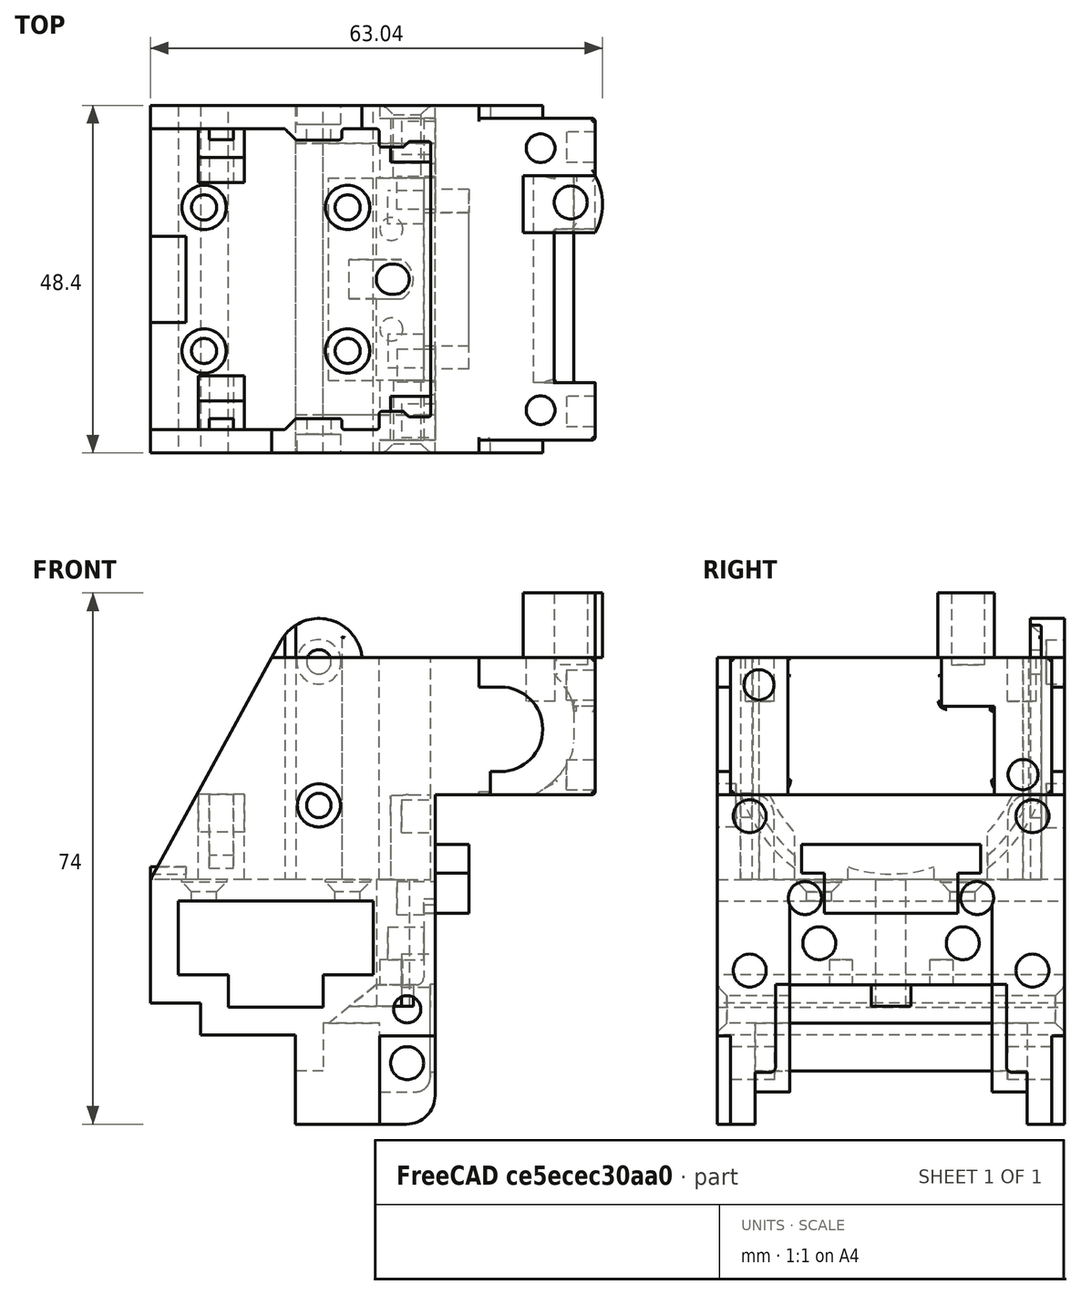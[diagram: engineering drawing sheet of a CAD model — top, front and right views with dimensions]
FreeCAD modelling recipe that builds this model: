
FCSTD DOCUMENT  (FreeCAD 1.0R38641 +468 (Git))
Label: k1_toolhead
License: All rights reserved
LicenseURL: https://en.wikipedia.org/wiki/All_rights_reserved
objects: App::Link×3, Part::Feature×1, PartDesign::FeatureBase×1, PartDesign::Body×1, App::Part×1
note: 4 computed .brp shape members not serialized (recipe doc carries the construction recipe); baked Part::Feature solids carry a one-line shape summary decoded from their .brp
EXTERNAL_REF file=cad_mgn12h_block.FCStd obj=Body
EXTERNAL_REF file=cad_extruder.FCStd obj=K1_Extruder_Assembly_v25
EXTERNAL_REF file=cad_hotend.FCStd obj=K1_Hotend

FEATURE [Part::Feature] Part__Feature  label="step"
  shape: bbox 63.04 x 48.4 x 74 mm, 296 faces (baked)
FEATURE [PartDesign::FeatureBase] BaseFeature
  BaseFeature = -> Part__Feature
  Suppressed = false
FEATURE [PartDesign::Body] Body  label="k1_toolhead"
  AllowCompound = false
  BaseFeature = -> Part__Feature
  Group = -> [BaseFeature]
  Origin = -> Origin001
  Tip = -> BaseFeature
FEATURE [App::Link] Link  label="cad_mgn12_link"
  LinkPlacement = pos=(-0.489994,-22.7,31.1) rot=(0.707107,0.707107,0;3.14159rad)
  LinkedObject = -> <external cad_mgn12h_block.FCStd>#Body
  Placement = pos=(-0.489994,-22.7,31.1) rot=(0.707107,0.707107,0;3.14159rad)
FEATURE [App::Link] Link001  label="cad_extruder_link"
  LinkPlacement = pos=(2.3,-0.3,53.5) rot=(0,0,1;1.5708rad)
  LinkedObject = -> <external cad_extruder.FCStd>#K1_Extruder_Assembly_v25
  Placement = pos=(2.3,-0.3,53.5) rot=(0,0,1;1.5708rad)
FEATURE [App::Link] Link002  label="cad_hotend_link"
  LinkedObject = -> <external cad_hotend.FCStd>#K1_Hotend
FEATURE [App::Part] Part  label="k1_toolhead_part"
  Group = -> [Body,Link,Link001,Link002]
  Origin = -> Origin

RESOLVED EXTERNAL PARTS (link-assembly join: the EXTERNAL_REF files above that resolve inside this repo's crawl, each included once):
---- part cad_mgn12h_block.FCStd = doc fcstd_671538b6926e ----
FCSTD DOCUMENT  (FreeCAD 1.0R38641 +468 (Git))
Label: cad_mgn12h_block
License: All rights reserved
LicenseURL: https://en.wikipedia.org/wiki/All_rights_reserved
objects: Sketcher::SketchObject×3, PartDesign::Pocket×2, PartDesign::Pad×1, PartDesign::Body×1
note: 16 computed .brp shape members not serialized (recipe doc carries the construction recipe); baked Part::Feature solids carry a one-line shape summary decoded from their .brp

FEATURE [Sketcher::SketchObject] Sketch
  ArcFitTolerance = 0
  AttachmentSupport = -> [YZ_Plane]
  FullyConstrained = true
  MakeInternals = false
  MapMode = 5
  Placement = pos=(0,0,0) rot=(0.57735,0.57735,0.57735;2.0944rad)
  sketch-geometry (4):
    g0: LineSegment StartX=13.5 StartY=0 StartZ=0 EndX=-13.5 EndY=-1e-16 EndZ=0
    g1: LineSegment StartX=-13.5 StartY=-1e-16 StartZ=0 EndX=-13.5 EndY=10 EndZ=0
    g2: LineSegment StartX=-13.5 StartY=10 StartZ=0 EndX=13.5 EndY=10 EndZ=0
    g3: LineSegment StartX=13.5 StartY=10 StartZ=0 EndX=13.5 EndY=0 EndZ=0
  constraints (11):
    c: Coincident(g0,g1)
    c: Coincident(g1,g2)
    c: Coincident(g2,g3)
    c: Coincident(g3,g0)
    c: Horizontal(g2)
    c: Vertical(g1)
    c: Vertical(g3)
    c: PointOnObject(g0,g-1)
    c: Symmetric(g0,g0,g-2)
    c: Distance(g2) = 27
    c: Distance(g1) = 10
FEATURE [PartDesign::Pad] Pad
  Direction = (1,0,0)
  Length = 45.4
  Length2 = 10
  Placement = pos=(0,0,0) rot=(1,1,1;2.0944rad)
  Profile = -> Sketch
  ReferenceAxis = -> Sketch [N_Axis]
  Suppressed = false
  Type = 0
FEATURE [Sketcher::SketchObject] Sketch001
  ArcFitTolerance = 0
  AttachmentSupport = -> [Pad]
  FullyConstrained = true
  MakeInternals = false
  MapMode = 5
  Placement = pos=(0,0,0) rot=(0.707107,0.707107,0;3.14159rad)
  sketch-geometry (8):
    g0: LineSegment [constr] StartX=-10 StartY=32.7 StartZ=0 EndX=10 EndY=32.7 EndZ=0
    g1: LineSegment [constr] StartX=10 StartY=32.7 StartZ=0 EndX=10 EndY=12.7 EndZ=0
    g2: LineSegment [constr] StartX=10 StartY=12.7 StartZ=0 EndX=-10 EndY=12.7 EndZ=0
    g3: LineSegment [constr] StartX=-10 StartY=12.7 StartZ=0 EndX=-10 EndY=32.7 EndZ=0
    g4: Circle CenterX=-10 CenterY=32.7 CenterZ=0 NormalX=0 NormalY=0 NormalZ=1 AngleXU=0 Radius=1.5
    g5: Circle CenterX=10 CenterY=32.7 CenterZ=0 NormalX=0 NormalY=0 NormalZ=1 AngleXU=0 Radius=1.5
    g6: Circle CenterX=10 CenterY=12.7 CenterZ=0 NormalX=0 NormalY=0 NormalZ=1 AngleXU=0 Radius=1.5
    g7: Circle CenterX=-10 CenterY=12.7 CenterZ=0 NormalX=0 NormalY=0 NormalZ=1 AngleXU=0 Radius=1.5
  constraints (19):
    c: Coincident(g0,g1)
    c: Coincident(g1,g2)
    c: Coincident(g2,g3)
    c: Coincident(g3,g0)
    c: Horizontal(g2)
    c: Vertical(g1)
    c: Vertical(g3)
    c: Symmetric(g0,g0,g-2)
    c: Distance(g0) = 20
    c: Distance(g1) = 20
    c: DistanceY(g-1,g2) = 12.7
    c: Coincident(g4,g0)
    c: Coincident(g5,g0)
    c: Coincident(g6,g1)
    c: Coincident(g7,g2)
    c: Equal(g7,g6)
    c: Equal(g6,g5)
    c: Equal(g5,g4)
    c: Radius(g4) = 1.5
FEATURE [PartDesign::Pocket] Pocket
  BaseFeature = -> Pad
  Direction = (0,0,1)
  Length = 5
  Length2 = 5
  Placement = pos=(0,0,0) rot=(1,1,1;2.0944rad)
  Profile = -> Sketch001
  ReferenceAxis = -> Sketch001 [N_Axis]
  Suppressed = false
  Type = 0
FEATURE [Sketcher::SketchObject] Sketch002
  ArcFitTolerance = 0
  AttachmentSupport = -> [Pocket]
  ExternalGeometry = -> [Pocket]
  FullyConstrained = true
  MakeInternals = false
  MapMode = 5
  Placement = pos=(0,0,0) rot=(0.57735,0.57735,-0.57735;4.18879rad)
  sketch-geometry (4):
    g0: LineSegment StartX=-6 StartY=-10 StartZ=0 EndX=6 EndY=-10 EndZ=0
    g1: LineSegment StartX=6 StartY=-10 StartZ=0 EndX=6 EndY=-5 EndZ=0
    g2: LineSegment StartX=6 StartY=-5 StartZ=0 EndX=-6 EndY=-5 EndZ=0
    g3: LineSegment StartX=-6 StartY=-5 StartZ=0 EndX=-6 EndY=-10 EndZ=0
  constraints (11):
    c: Coincident(g0,g1)
    c: Coincident(g1,g2)
    c: Coincident(g2,g3)
    c: Coincident(g3,g0)
    c: Horizontal(g0)
    c: Vertical(g1)
    c: Vertical(g3)
    c: PointOnObject(g0,g-3)
    c: Symmetric(g2,g1,g-2)
    c: Distance(g1) = 5
    c: Distance(g2) = 12
FEATURE [PartDesign::Pocket] Pocket001
  BaseFeature = -> Pocket
  Direction = (1,0,0)
  Length = 5
  Length2 = 5
  Placement = pos=(0,0,0) rot=(1,1,1;2.0944rad)
  Profile = -> Sketch002
  ReferenceAxis = -> Sketch002 [N_Axis]
  Suppressed = false
  Type = 1
FEATURE [PartDesign::Body] Body  label="mgn12h_block"
  AllowCompound = false
  Group = -> [Sketch,Pad,Sketch001,Pocket,Sketch002,Pocket001]
  Origin = -> Origin
  Placement = pos=(0,13.5,0) rot=(0,0,1;0rad)
  Tip = -> Pocket001
